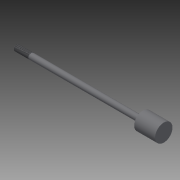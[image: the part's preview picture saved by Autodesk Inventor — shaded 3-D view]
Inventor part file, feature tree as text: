
AUTODESK INVENTOR PART (.ipt)
format: ipt  version: 2014 (Build 180170000, 170)  size: 124,416 bytes
history: native  units: in
note: dims shown in document units (in); Inventor stores cm internally (conversion verified against a paired STEP export)
features: other x49, revolve x3, sketch x3, thread x1
ambient origin geometry x8: Origin, YZ Plane, XZ Plane, XY Plane, X Axis, Y Axis, Z Axis, Center Point
bodies: Solid1 (feature_tree)
feature tree (56):
  revolve  "Revolution1"  [1 undecoded]
  thread  "Thread1"  [1 undecoded]
  revolve  "Revolution2"  [1 undecoded]
  revolve  "Revolution3"  [1 undecoded]
  other  "h1_XY"
  other  "h1_YZ"
  other  "h1_ZX"
  other  "h1_X"
  other  "h1_Y"
  other  "h1_Z"
  other  "h1_Center"
  other  "h2_XY"
  other  "h2_YZ"
  other  "h2_ZX"
  other  "h2_X"
  other  "h2_Y"
  other  "h2_Z"
  other  "h2_Center"
  other  "k1_XY"
  other  "k1_YZ"
  other  "k1_ZX"
  other  "k1_X"
  other  "k1_Y"
  other  "k1_Z"
  other  "k1_Center"
  other  "k2_XY"
  other  "k2_YZ"
  other  "k2_ZX"
  other  "k2_X"
  other  "k2_Y"
  other  "k2_Z"
  other  "k2_Center"
  other  "start_XY"
  other  "start_YZ"
  other  "start_ZX"
  other  "start_X"
  other  "start_Y"
  other  "start_Z"
  other  "start_Center"
  other  "to_prc_XY"
  other  "to_prc_YZ"
  other  "to_prc_ZX"
  other  "to_prc_X"
  other  "to_prc_Y"
  other  "to_prc_Z"
  other  "to_prc_Center"
  other  "to_rod_guide_XY"
  other  "to_rod_guide_YZ"
  other  "to_rod_guide_ZX"
  other  "to_rod_guide_X"
  other  "to_rod_guide_Y"
  other  "to_rod_guide_Z"
  other  "to_rod_guide_Center"
  sketch  "Sketch_3"  dims[d0=360.0deg d1=0.49in d2=4.291in d3=360.0deg]
  sketch  "Sketch_17"
  sketch  "Sketch_12"  dims[d4=360.0deg]
note: 4 required parameter values undecoded (feature->parameter linkage not recoverable at this tier; creation-order binding heuristic only, values carry confidence <= 0.55)